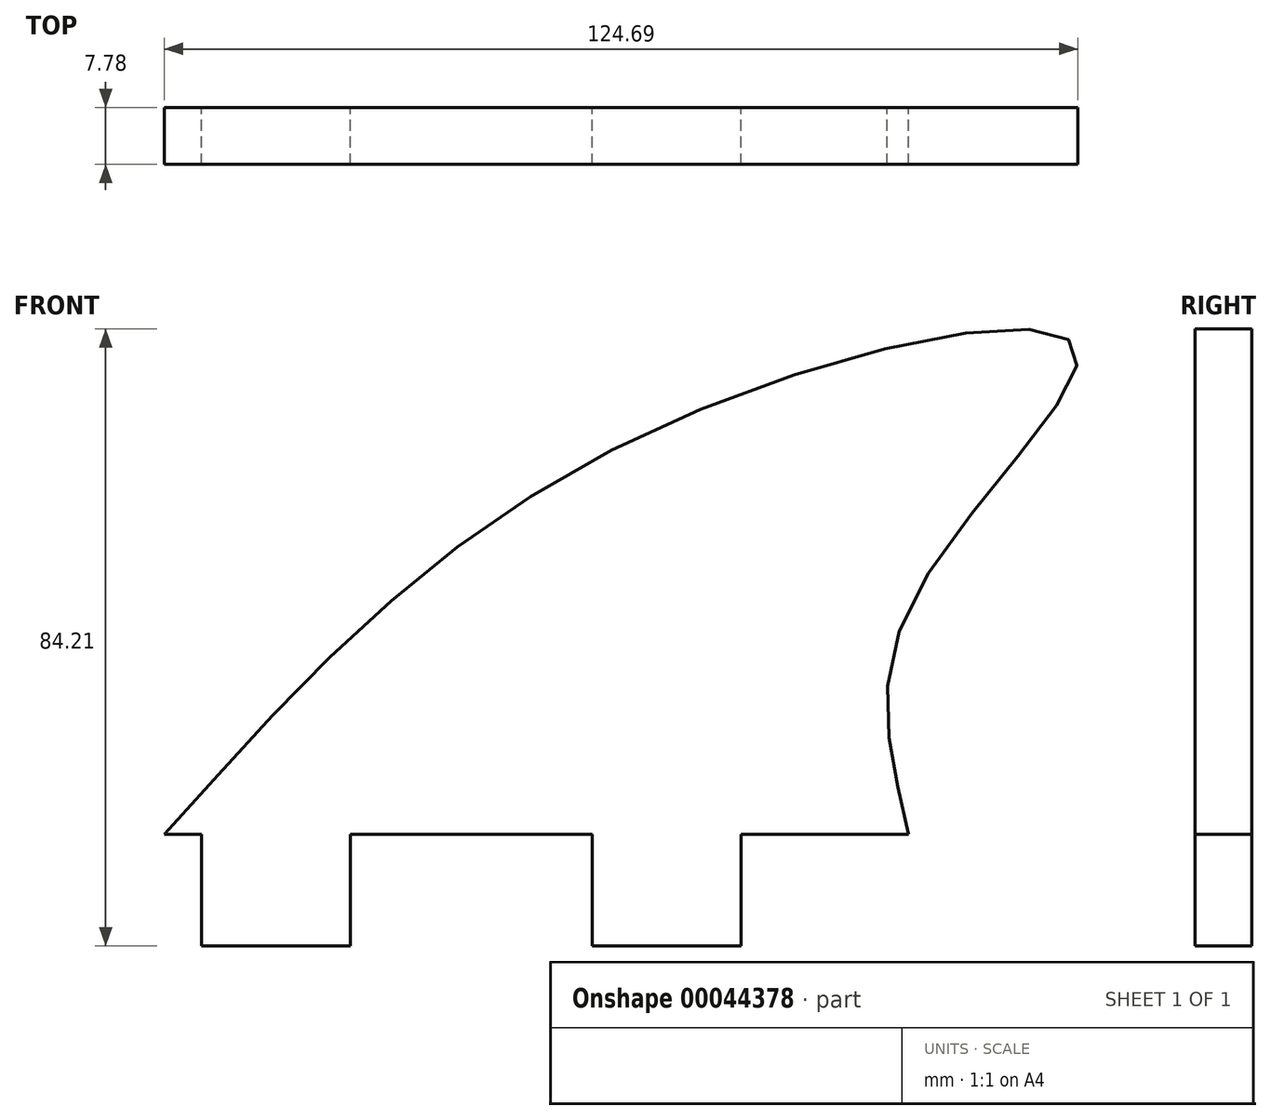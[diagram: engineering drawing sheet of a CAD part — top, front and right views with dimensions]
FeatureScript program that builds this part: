
annotation { "Feature Type Name" : "Feature", "Feature Type Description" : "" }
export const myFeature = defineFeature(function(context is Context, id is Id, definition is map)
    precondition{}
    {
        {
            var Q0;
            Q0=qCreatedBy(makeId("Front.planeOp"),FACE);
            var sketch = newSketch(context, id + "F0", { "sketchPlane" : qUnion([Q0])});
            skLineSegment(sketch, "E0", {"start": v(-34.33, -38.52) * mm, "end": v(-29.25, -38.52) * mm});
            skLineSegment(sketch, "E1", {"start": v(-29.25, -38.52) * mm, "end": v(-29.25, -53.76) * mm});
            skLineSegment(sketch, "E2", {"start": v(-29.25, -53.76) * mm, "end": v(-8.93, -53.76) * mm});
            skLineSegment(sketch, "E3", {"start": v(-8.93, -53.76) * mm, "end": v(-8.93, -38.52) * mm});
            skLineSegment(sketch, "E4", {"start": v(-8.93, -38.52) * mm, "end": v(24.09, -38.52) * mm});
            skLineSegment(sketch, "E5", {"start": v(24.09, -38.52) * mm, "end": v(24.09, -53.76) * mm});
            skLineSegment(sketch, "E6", {"start": v(24.09, -53.76) * mm, "end": v(44.4, -53.76) * mm});
            skLineSegment(sketch, "E7", {"start": v(44.4, -53.76) * mm, "end": v(44.4, -38.52) * mm});
            skLineSegment(sketch, "E8", {"start": v(44.4, -38.52) * mm, "end": v(67.27, -38.52) * mm});
            skFitSpline(sketch, "E9", {"points": [v(67.27, -38.52) * mm, v(67.27, -7.77) * mm, v(90.18, 27.63) * mm, v(29.33, 15.22) * mm, v(-34.33, -38.52) * mm], "startDerivative": vector(-32.02, 146.65) * mm, "endDerivative": vector(-168.4, -186.3) * mm});
            skSolve(sketch);
        }
        {
            var Q0;
            Q0=makeQuery(id+"F0.imprint","IMPRINT",FACE,{"disambiguationData":[TD([[makeQuery(id+"F0.imprint","IMPRINT",EDGE,{"derivedFrom":sQuery(id+"F0.wireOp",EDGE,"E0")}),1.0]])]});
            extrude(context, id + "F1", {"entities" : qUnion([Q0]), "depth" : 7.78 * mm});
        }
    });
